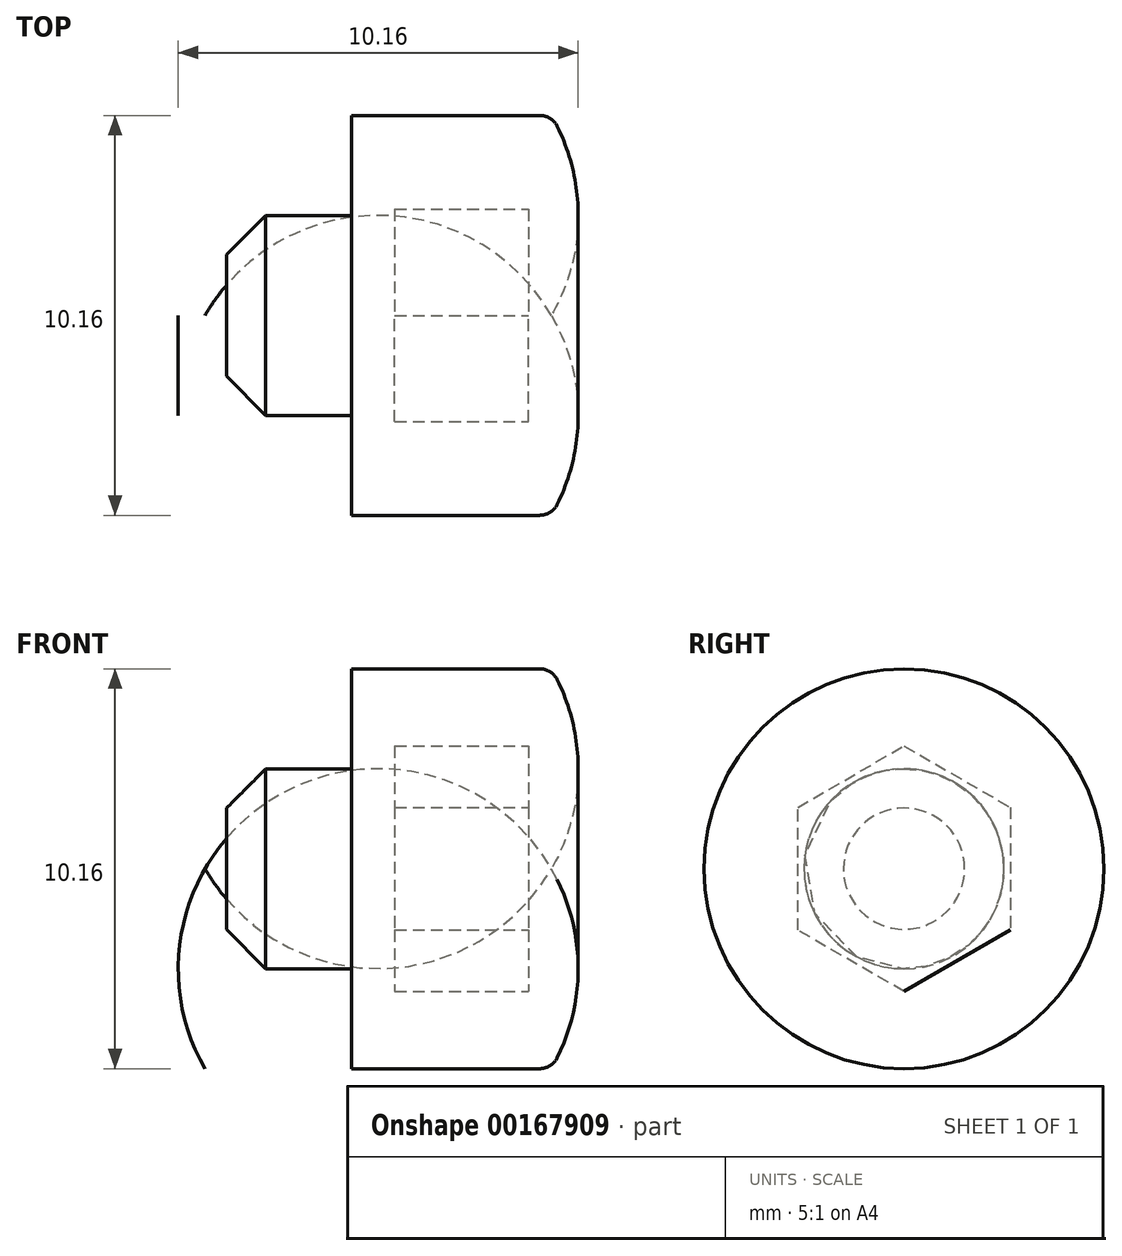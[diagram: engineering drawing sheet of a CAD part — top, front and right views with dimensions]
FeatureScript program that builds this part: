
annotation { "Feature Type Name" : "Feature", "Feature Type Description" : "" }
export const myFeature = defineFeature(function(context is Context, id is Id, definition is map)
    precondition{}
    {
        {
            var Q0;
            Q0=qCreatedBy(makeId("Front.planeOp"),FACE);
            var sketch = newSketch(context, id + "F0", { "sketchPlane" : qUnion([Q0])});
            skLineSegment(sketch, "E0", {"start": v(0, 2.54) * mm, "end": v(0, 5.08) * mm});
            skLineSegment(sketch, "E1", {"start": v(0, 5.08) * mm, "end": v(5.08, 5.08) * mm});
            skLineSegment(sketch, "E2", {"start": v(0, 2.54) * mm, "end": v(-3.17, 2.54) * mm});
            skLineSegment(sketch, "E3", {"start": v(-3.17, 2.54) * mm, "end": v(-3.17, 0) * mm});
            skLineSegment(sketch, "E4", {"start": v(-3.17, 0) * mm, "end": v(5.08, 0) * mm});
            skArc(sketch, "E5", {"start": v(5.08, 0) * mm, "mid": v(5.76, 2.54) * mm, "end": v(5.08, 5.08) * mm});
            skLineSegment(sketch, "E6", {"start": v(-3.18, 0) * mm, "end": v(-45.57, 0) * mm, "construction": true});
            skSolve(sketch);
        }
        {
            var Q0;
            Q0=makeQuery(id+"F0.imprint","IMPRINT",FACE,{"disambiguationData":[TD([[makeQuery(id+"F0.imprint","IMPRINT",EDGE,{"derivedFrom":sQuery(id+"F0.wireOp",EDGE,"E0")}),-1.0]])]});
            var Q1;
            Q1=sQuery(id+"F0.wireOp",EDGE,"E6");
            revolve(context, id + "F1", {"entities" : qUnion([Q0]), "axis" : qUnion([Q1]), "revolveType" : RevolveType.FULL});
        }
        {
            var Q0;
            Q0=makeQuery(id+"F1.opRevolve","SWEPT_EDGE",EDGE,{"disambiguationData":[OSD([sQuery(id+"F0.wireOp",EDGE,"E2"),sQuery(id+"F0.wireOp",EDGE,"E3")])]});
            chamfer(context, id + "F2", {"entities" : qUnion([Q0]), "width" : 1 * mm, "tangentPropagation" : true});
        }
        {
            var Q0;
            Q0=makeQuery(id+"F1.opRevolve","SWEPT_EDGE",EDGE,{"disambiguationData":[OSD([sQuery(id+"F0.wireOp",EDGE,"E1"),sQuery(id+"F0.wireOp",EDGE,"E5")])]});
            fillet(context, id + "F3", {"entities" : qUnion([Q0]), "radius" : .5 * mm, "tangentPropagation" : true, "allowEdgeOverflow" : false});
        }
        {
            var Q0;
            Q0=qCreatedBy(makeId("Right.planeOp"),FACE);
            cPlane(context, id + "F4", {"entities" : qUnion([Q0]), "cplaneType" : CPlaneType.OFFSET, "offset" : 4.5 * mm, "width" : 150 * mm, "height" : 150 * mm});
        }
        {
            var Q0;
            Q0=qCreatedBy(id+"F4.planeOp",FACE);
            var sketch = newSketch(context, id + "F5", { "sketchPlane" : qUnion([Q0])});
            skCircle(sketch, "E7.cCircle", {"center": v(0, 0) * mm, "radius": 2.7 * mm, "construction": true});
            skLineSegment(sketch, "E7.0", {"start": v(2.7, -1.56) * mm, "end": v(0, -3.12) * mm});
            skLineSegment(sketch, "E7.1", {"start": v(0, -3.12) * mm, "end": v(-2.7, -1.56) * mm});
            skLineSegment(sketch, "E7.2", {"start": v(-2.7, -1.56) * mm, "end": v(-2.7, 1.56) * mm});
            skLineSegment(sketch, "E7.3", {"start": v(-2.7, 1.56) * mm, "end": v(0, 3.12) * mm});
            skLineSegment(sketch, "E7.4", {"start": v(0, 3.12) * mm, "end": v(2.7, 1.56) * mm});
            skLineSegment(sketch, "E7.5", {"start": v(2.7, 1.56) * mm, "end": v(2.7, -1.56) * mm});
            skPoint(sketch, "E7.0.midPoint", {"position": v(1.35, -2.34) * mm});
            skSolve(sketch);
        }
        {
            var Q0;
            Q0=makeQuery(id+"F5.imprint","IMPRINT",FACE,{"disambiguationData":[TD([[makeQuery(id+"F5.imprint","IMPRINT",EDGE,{"derivedFrom":sQuery(id+"F5.wireOp",EDGE,"E7.0")}),-1.0]])]});
            extrude(context, id + "F6", {"entities" : qUnion([Q0]), "operationType" : NewBodyOperationType.REMOVE, "oppositeDirection" : true, "depth" : 3.4 * mm});
        }
    });
